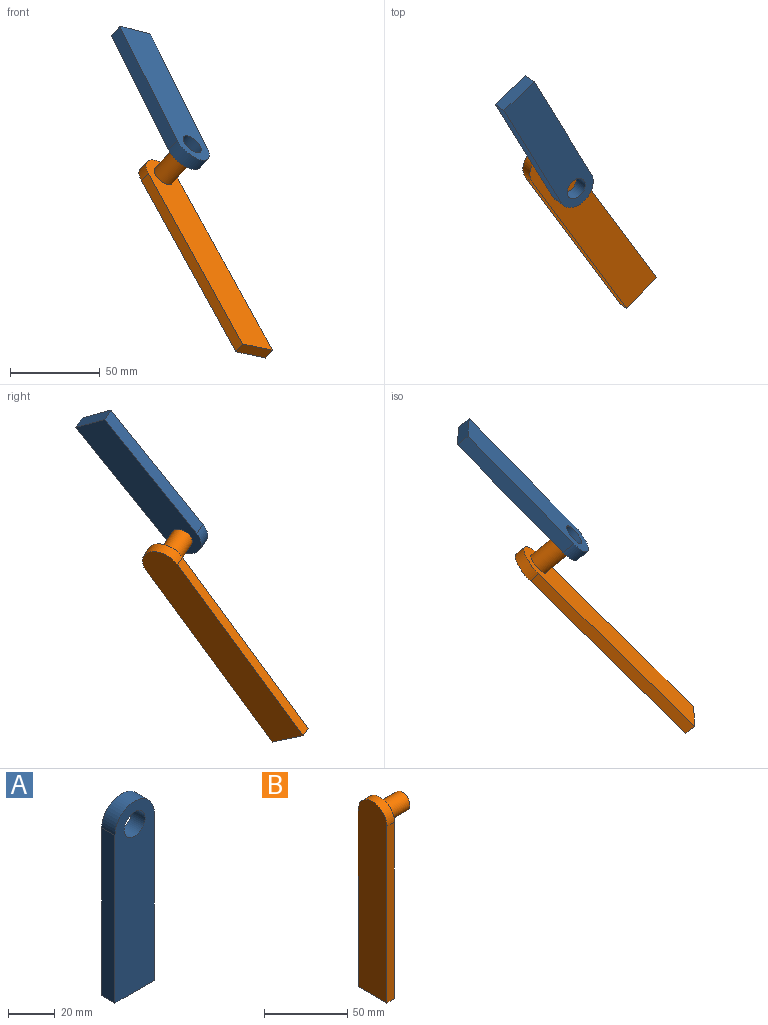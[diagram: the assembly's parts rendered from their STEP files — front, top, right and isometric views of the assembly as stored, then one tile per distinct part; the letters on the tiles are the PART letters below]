
ASSEMBLY  parts=2 mates=1
PART A: 7 faces, bbox 23.8x8x99.8 mm
  f0: plane 23.79x7.99mm, normal (0,0,-1), area 190mm2, adj f1,f3,f5,f6
  f1: plane 87.89x7.99mm, normal (1,0,0), area 702.1mm2, adj f0,f2,f5,f6
  f2: cylinder r=11.9mm len=23.79mm, axis (0,1,0), area 298.5mm2, adj f1,f3,f5,f6
  f3: plane 87.89x7.99mm, normal (-1,0,0), area 702.1mm2, adj f0,f2,f5,f6
  f4: cylinder r=6.35mm len=12.7mm, axis (0,1,0), area 318.7mm2, adj f5,f6
  f5: plane 99.79x23.79mm, normal (0,-1,0), area 2186.6mm2, adj f0,f1,f2,f3,f4
  f6: plane 99.79x23.79mm, normal (0,1,0), area 2186.6mm2, adj f0,f1,f2,f3,f4
PART B: 8 faces, bbox 25.4x24.2x141.8 mm
  f0: cylinder r=6.35mm len=18.88mm, axis (-1,0,0), area 753.4mm2, adj f1,f6
  f1: plane 12.7x12.7mm, normal (1,0,0), area 126.7mm2, adj f0
  f2: plane 129.69x6.52mm, normal (0,-1,0), area 845.2mm2, adj f3,f5,f6,f7
  f3: plane 24.25x6.52mm, normal (0,0,-1), area 158mm2, adj f2,f4,f6,f7
  f4: plane 129.69x6.52mm, normal (0,1,0), area 845.2mm2, adj f3,f5,f6,f7
  f5: cylinder r=12.12mm len=24.25mm, axis (-1,0,0), area 248.2mm2, adj f2,f4,f6,f7
  f6: plane 141.81x24.25mm, normal (1,0,0), area 3249mm2, adj f0,f2,f3,f4,f5
  f7: plane 141.81x24.25mm, normal (-1,0,0), area 3375.7mm2, adj f2,f3,f4,f5
PLACE A rot(axis=(-0.38,0.85,-0.37),174.1deg) t=(56.68,-110.5,178.9)mm
PLACE B rot(axis=(-0.4,-0.63,-0.67),58.3deg) t=(135.48,-145.6,45.06)mm
MATE revolute B.f0 <-> A.f2  axis (0.6,-0.45,0.66) through (101.79,-134.17,121.85)mm
